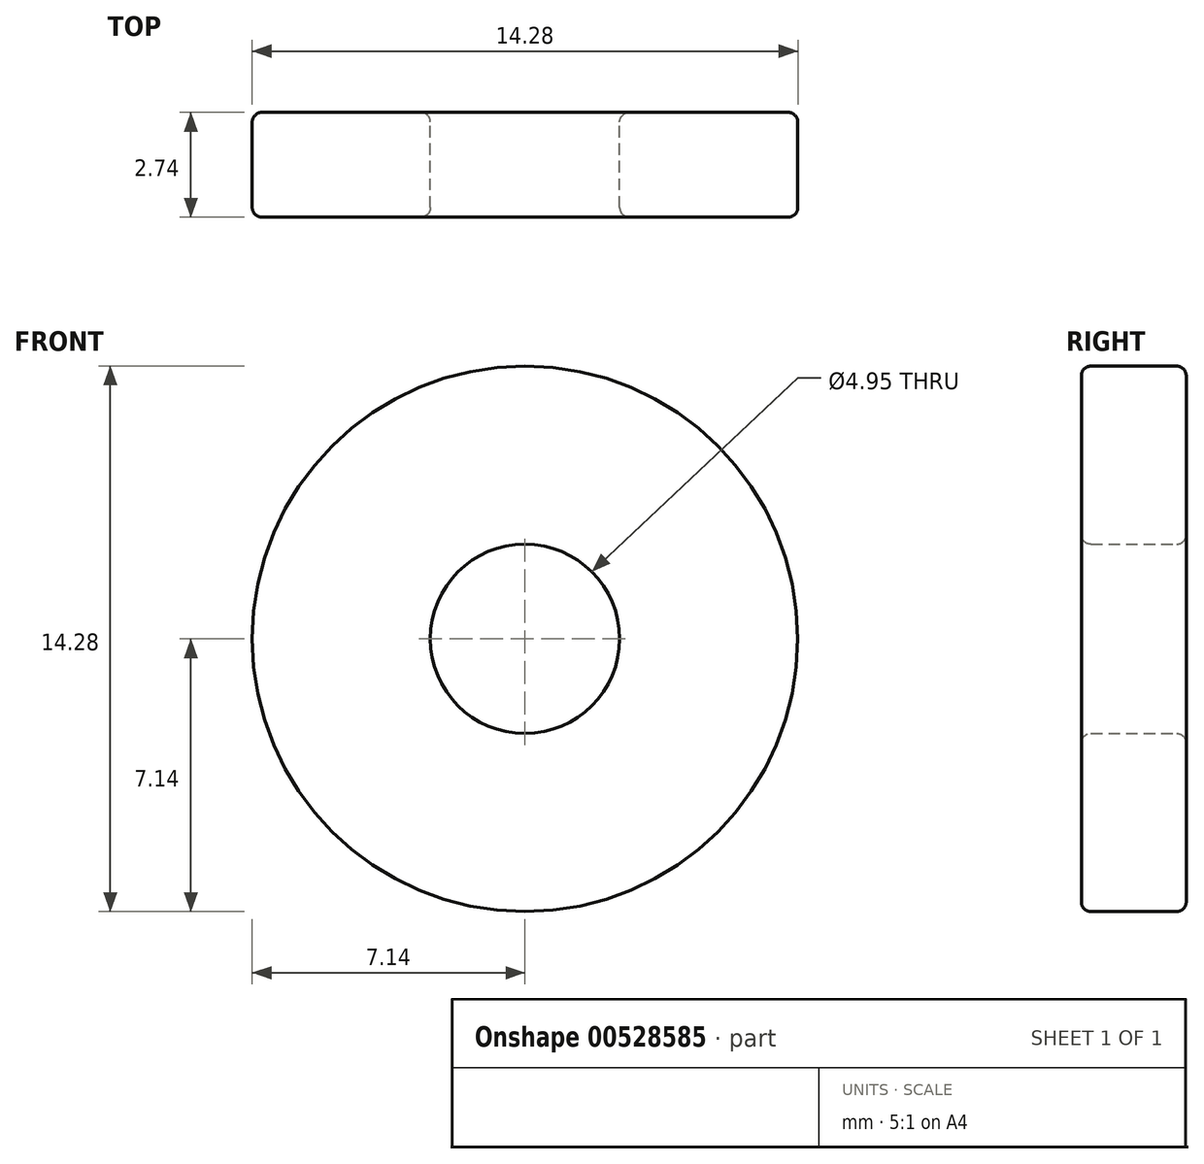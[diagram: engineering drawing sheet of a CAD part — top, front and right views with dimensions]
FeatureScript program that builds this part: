
annotation { "Feature Type Name" : "Feature", "Feature Type Description" : "" }
export const myFeature = defineFeature(function(context is Context, id is Id, definition is map)
    precondition{}
    {
        {
            var Q0;
            Q0=qCreatedBy(makeId("Front.planeOp"),FACE);
            var sketch = newSketch(context, id + "F0", { "sketchPlane" : qUnion([Q0])});
            skCircle(sketch, "E0", {"center": v(0, 0) * mm, "radius": 2.48 * mm});
            skCircle(sketch, "E1", {"center": v(0, 0) * mm, "radius": 7.14 * mm});
            skSolve(sketch);
        }
        {
            var Q0;
            Q0 = qSketchRegion(id + "F0", true);
            extrude(context, id + "F1", {"entities" : qUnion([Q0]), "depth" : 2.74 * mm, "offsetDistance" : 25 * mm});
        }
        {
            var Q0;
            Q0=makeQuery(id+"F1.opExtrude","CAP_EDGE",EDGE,{"disambiguationData":[OSD([sQuery(id+"F0.wireOp",EDGE,"E1")])],"isStart":false});
            var Q1;
            Q1=makeQuery(id+"F1.opExtrude","CAP_EDGE",EDGE,{"disambiguationData":[OSD([sQuery(id+"F0.wireOp",EDGE,"E0")])],"isStart":false});
            var Q2;
            Q2=makeQuery(id+"F1.opExtrude","CAP_EDGE",EDGE,{"disambiguationData":[OSD([sQuery(id+"F0.wireOp",EDGE,"E1")])],"isStart":true});
            var Q3;
            Q3=makeQuery(id+"F1.opExtrude","CAP_EDGE",EDGE,{"disambiguationData":[OSD([sQuery(id+"F0.wireOp",EDGE,"E0")])],"isStart":true});
            fillet(context, id + "F2", {"entities" : qUnion([Q0, Q1, Q2, Q3]), "radius" : .25 * mm, "tangentPropagation" : true, "allowEdgeOverflow" : false});
        }
    });
